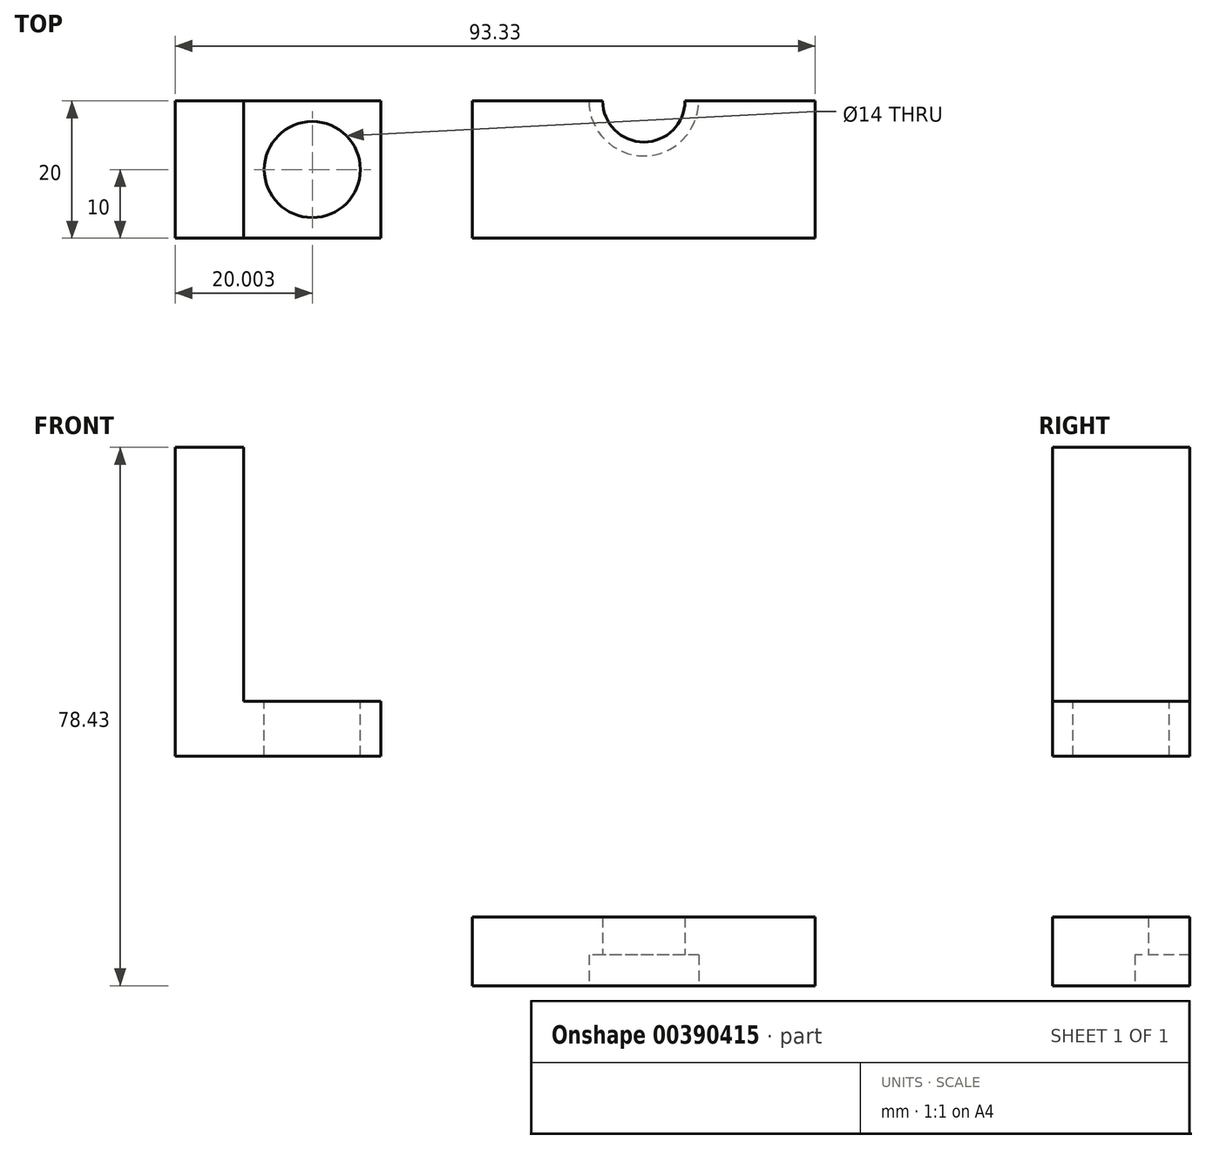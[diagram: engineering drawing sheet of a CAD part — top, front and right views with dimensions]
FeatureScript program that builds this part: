
annotation { "Feature Type Name" : "Feature", "Feature Type Description" : "" }
export const myFeature = defineFeature(function(context is Context, id is Id, definition is map)
    precondition{}
    {
        {
            var Q0;
            Q0=qCreatedBy(makeId("Top.planeOp"),FACE);
            var sketch = newSketch(context, id + "F0", { "sketchPlane" : qUnion([Q0])});
            skLineSegment(sketch, "E0.bottom", {"start": v(-21.96, 20) * mm, "end": v(28.04, 20) * mm});
            skLineSegment(sketch, "E0.top", {"start": v(-21.96, 0) * mm, "end": v(28.04, 0) * mm});
            skLineSegment(sketch, "E0.left", {"start": v(-21.96, 20) * mm, "end": v(-21.96, 0) * mm});
            skLineSegment(sketch, "E0.right", {"start": v(28.04, 20) * mm, "end": v(28.04, 0) * mm});
            skArc(sketch, "E1", {"start": v(-2.96, 20) * mm, "mid": v(3.04, 14) * mm, "end": v(9.04, 20) * mm});
            skSolve(sketch);
        }
        {
            var Q0;
            Q0=makeQuery(id+"F0.imprint","IMPRINT",FACE,{"disambiguationData":[TD([[makeQuery(id+"F0.imprint","IMPRINT",EDGE,{"derivedFrom":sQuery(id+"F0.wireOp",EDGE,"E0.top")}),1.0]])]});
            extrude(context, id + "F1", {"entities" : qUnion([Q0]), "depth" : 10 * mm});
        }
        {
            var Q0;
            Q0=makeQuery(id+"F1.opExtrude","CAP_FACE",FACE,{"disambiguationData":[OSD([sQuery(id+"F0.wireOp",EDGE,"E0.bottom"),sQuery(id+"F0.wireOp",EDGE,"E0.top"),sQuery(id+"F0.wireOp",EDGE,"E0.left"),sQuery(id+"F0.wireOp",EDGE,"E0.right"),sQuery(id+"F0.wireOp",EDGE,"E1")])],"isStart":true});
            var sketch = newSketch(context, id + "F2", { "sketchPlane" : qUnion([Q0])});
            skArc(sketch, "E2", {"start": v(11.04, -20) * mm, "mid": v(3.04, -12) * mm, "end": v(-4.96, -20) * mm});
            skLineSegment(sketch, "E3", {"start": v(28.04, -20) * mm, "end": v(-21.96, -20) * mm});
            skSolve(sketch);
        }
        {
            var Q0;
            Q0 = qSketchRegion(id + "F2", true);
            extrude(context, id + "F3", {"entities" : qUnion([Q0]), "operationType" : NewBodyOperationType.REMOVE, "oppositeDirection" : true, "depth" : 4.5 * mm});
        }
        {
            var Q0;
            Q0=qCreatedBy(makeId("Front.planeOp"),FACE);
            var sketch = newSketch(context, id + "F4", { "sketchPlane" : qUnion([Q0])});
            skLineSegment(sketch, "E4", {"start": v(-65.29, 78.43) * mm, "end": v(-55.29, 78.43) * mm});
            skLineSegment(sketch, "E5", {"start": v(-55.29, 78.43) * mm, "end": v(-55.29, 41.43) * mm});
            skLineSegment(sketch, "E6", {"start": v(-55.29, 41.43) * mm, "end": v(-35.29, 41.43) * mm});
            skLineSegment(sketch, "E7", {"start": v(-35.29, 41.43) * mm, "end": v(-35.29, 33.43) * mm});
            skLineSegment(sketch, "E8", {"start": v(-35.29, 33.43) * mm, "end": v(-65.29, 33.43) * mm});
            skLineSegment(sketch, "E9", {"start": v(-65.29, 33.43) * mm, "end": v(-65.29, 78.43) * mm});
            skSolve(sketch);
        }
        {
            var Q0;
            Q0=makeQuery(id+"F4.imprint","IMPRINT",FACE,{"disambiguationData":[TD([[makeQuery(id+"F4.imprint","IMPRINT",EDGE,{"derivedFrom":sQuery(id+"F4.wireOp",EDGE,"E4")}),-1.0]])]});
            extrude(context, id + "F5", {"entities" : qUnion([Q0]), "oppositeDirection" : true, "depth" : 20 * mm});
        }
        {
            var Q0;
            Q0=makeQuery(id+"F5.opExtrude","SWEPT_FACE",FACE,{"disambiguationData":[OSD([sQuery(id+"F4.wireOp",EDGE,"E6")])]});
            var sketch = newSketch(context, id + "F6", { "sketchPlane" : qUnion([Q0])});
            skCircle(sketch, "E10", {"center": v(-45.29, 10) * mm, "radius": 7 * mm});
            skLineSegment(sketch, "E11", {"start": v(-45.29, 0) * mm, "end": v(-45.29, 20) * mm, "construction": true});
            skLineSegment(sketch, "E12", {"start": v(-55.29, 10) * mm, "end": v(-35.29, 10) * mm, "construction": true});
            skSolve(sketch);
        }
        {
            var Q0;
            Q0 = qSketchRegion(id + "F6", true);
            extrude(context, id + "F7", {"entities" : qUnion([Q0]), "operationType" : NewBodyOperationType.REMOVE, "oppositeDirection" : true, "depth" : 25 * mm});
        }
    });
